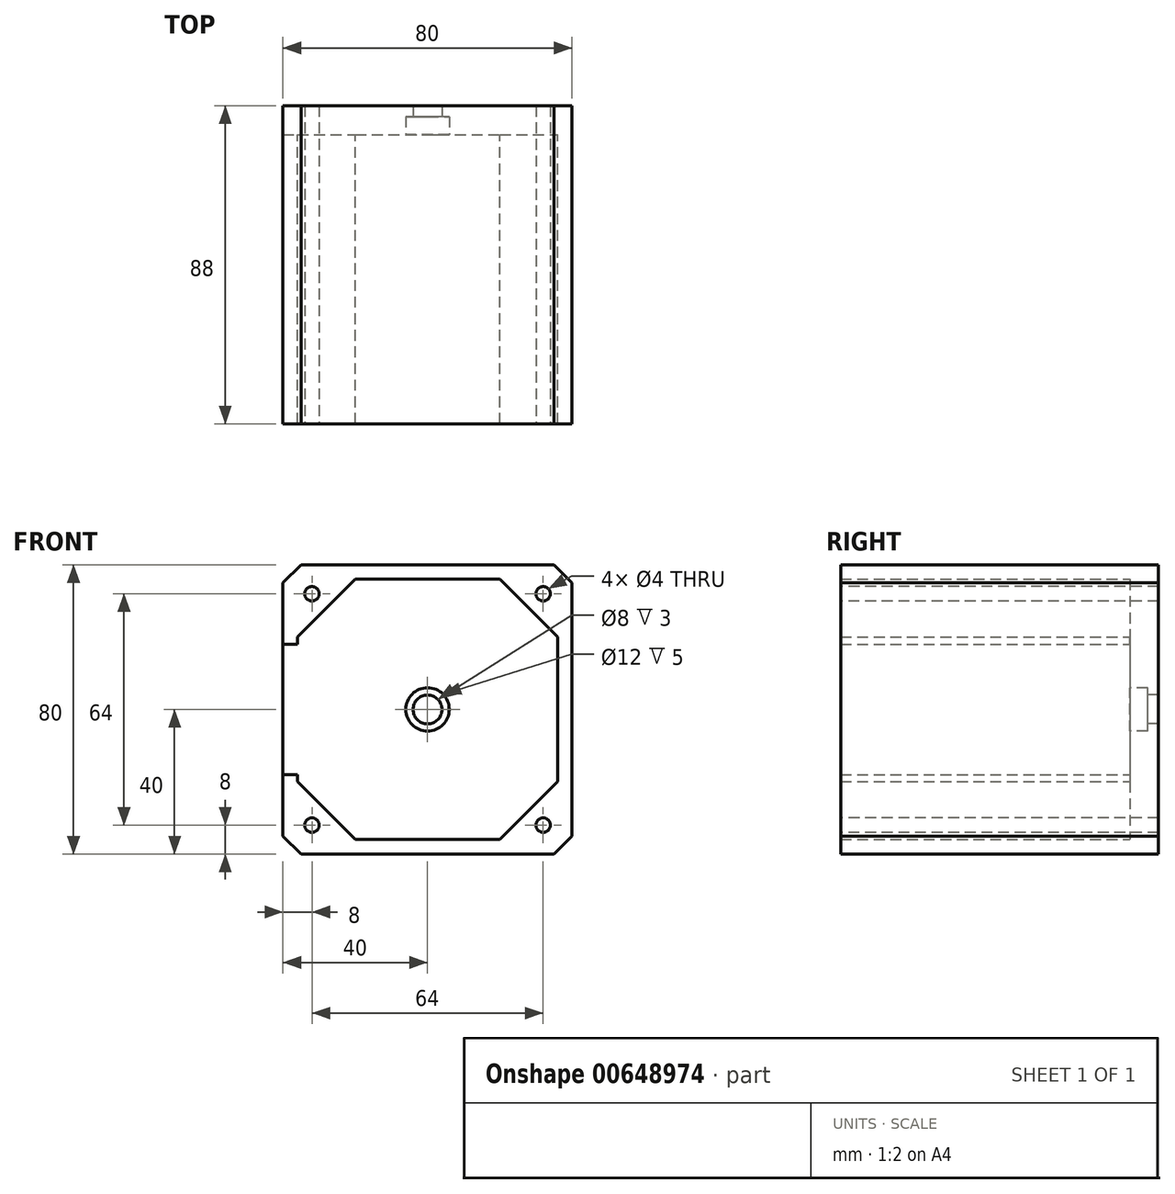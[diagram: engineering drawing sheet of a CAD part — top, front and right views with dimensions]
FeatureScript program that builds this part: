
annotation { "Feature Type Name" : "Feature", "Feature Type Description" : "" }
export const myFeature = defineFeature(function(context is Context, id is Id, definition is map)
    precondition{}
    {
        {
            var Q0;
            Q0=qCreatedBy(makeId("Front.planeOp"),FACE);
            var sketch = newSketch(context, id + "F0", { "sketchPlane" : qUnion([Q0])});
            skLineSegment(sketch, "E0.bottom", {"start": v(-40, 40) * mm, "end": v(40, 40) * mm});
            skLineSegment(sketch, "E0.top", {"start": v(-40, -40) * mm, "end": v(40, -40) * mm});
            skLineSegment(sketch, "E0.left", {"start": v(-40, 40) * mm, "end": v(-40, -40) * mm});
            skLineSegment(sketch, "E0.right", {"start": v(40, 40) * mm, "end": v(40, -40) * mm});
            skPoint(sketch, "E0.middle", {"position": v(0, 0) * mm});
            skSolve(sketch);
        }
        {
            var Q0;
            Q0 = qSketchRegion(id + "F0", true);
            extrude(context, id + "F1", {"entities" : qUnion([Q0]), "depth" : 8 * mm, "offsetDistance" : 25 * mm});
        }
        {
            var Q0;
            Q0=makeQuery(id+"F1.opExtrude","CAP_FACE",FACE,{"disambiguationData":[OSD([sQuery(id+"F0.wireOp",EDGE,"E0.bottom"),sQuery(id+"F0.wireOp",EDGE,"E0.top"),sQuery(id+"F0.wireOp",EDGE,"E0.left"),sQuery(id+"F0.wireOp",EDGE,"E0.right")])],"isStart":false});
            var sketch = newSketch(context, id + "F2", { "sketchPlane" : qUnion([Q0])});
            skCircle(sketch, "E1", {"center": v(0, 0) * mm, "radius": 4 * mm});
            skSolve(sketch);
        }
        {
            var Q0;
            Q0 = qSketchRegion(id + "F2", true);
            extrude(context, id + "F3", {"entities" : qUnion([Q0]), "operationType" : NewBodyOperationType.REMOVE, "endBound" : BoundingType.THROUGH_ALL, "oppositeDirection" : true, "depth" : 25 * mm, "offsetDistance" : 25 * mm});
        }
        {
            var Q0;
            Q0=makeQuery(id+"F1.opExtrude","CAP_FACE",FACE,{"disambiguationData":[OSD([sQuery(id+"F0.wireOp",EDGE,"E0.bottom"),sQuery(id+"F0.wireOp",EDGE,"E0.top"),sQuery(id+"F0.wireOp",EDGE,"E0.left"),sQuery(id+"F0.wireOp",EDGE,"E0.right")])],"isStart":false});
            var sketch = newSketch(context, id + "F4", { "sketchPlane" : qUnion([Q0])});
            skLineSegment(sketch, "E2.bottom", {"start": v(-40, 40) * mm, "end": v(40, 40) * mm});
            skLineSegment(sketch, "E2.top", {"start": v(-40, -40) * mm, "end": v(40, -40) * mm});
            skLineSegment(sketch, "E2.left", {"start": v(-40, 40) * mm, "end": v(-40, 18) * mm});
            skLineSegment(sketch, "E2.right", {"start": v(40, 40) * mm, "end": v(40, -40) * mm});
            skPoint(sketch, "E2.middle", {"position": v(0, 0) * mm});
            skLineSegment(sketch, "E3", {"start": v(-40, 18) * mm, "end": v(-36, 18) * mm});
            skLineSegment(sketch, "E4", {"start": v(-40, 0) * mm, "end": v(0, 0) * mm, "construction": true});
            skLineSegment(sketch, "E5", {"start": v(-36, 18) * mm, "end": v(-36, 20) * mm});
            skLineSegment(sketch, "E6", {"start": v(-36, 20) * mm, "end": v(-20, 36) * mm});
            skLineSegment(sketch, "E7", {"start": v(-20, 36) * mm, "end": v(20, 36) * mm});
            skLineSegment(sketch, "E8", {"start": v(20, 36) * mm, "end": v(36, 20) * mm});
            skLineSegment(sketch, "E9", {"start": v(36, 20) * mm, "end": v(36, 0) * mm});
            skLineSegment(sketch, "E10", {"start": v(36, 0) * mm, "end": v(0, 0) * mm, "construction": true});
            skLineSegment(sketch, "E11.MirrorCS", {"start": v(-40, -18) * mm, "end": v(-36, -18) * mm});
            skLineSegment(sketch, "E12.MirrorCS", {"start": v(-36, -18) * mm, "end": v(-36, -20) * mm});
            skLineSegment(sketch, "E13.MirrorCS", {"start": v(-36, -20) * mm, "end": v(-20, -36) * mm});
            skLineSegment(sketch, "E14.MirrorCS", {"start": v(-20, -36) * mm, "end": v(20, -36) * mm});
            skLineSegment(sketch, "E15.MirrorCS", {"start": v(36, -20) * mm, "end": v(36, 0) * mm});
            skLineSegment(sketch, "E16.MirrorCS", {"start": v(20, -36) * mm, "end": v(36, -20) * mm});
            skLineSegment(sketch, "E17.trimOffspring", {"start": v(-40, -18) * mm, "end": v(-40, -40) * mm});
            skSolve(sketch);
        }
        {
            var Q0;
            Q0 = qSketchRegion(id + "F4", true);
            extrude(context, id + "F5", {"entities" : qUnion([Q0]), "operationType" : NewBodyOperationType.ADD, "depth" : 80 * mm, "offsetDistance" : 25 * mm});
        }
        {
            var Q0;
            Q0=makeQuery(id+"F5.boolean.opBoolean","MERGE",EDGE,{"derivedFrom":[makeQuery(id+"F1.opExtrude","SWEPT_EDGE",EDGE,{"disambiguationData":[OSD([sQuery(id+"F0.wireOp",EDGE,"E0.bottom"),sQuery(id+"F0.wireOp",EDGE,"E0.left")])]}),makeQuery(id+"F5.opExtrude","SWEPT_EDGE",EDGE,{"disambiguationData":[OSD([sQuery(id+"F4.wireOp",EDGE,"E2.bottom"),sQuery(id+"F4.wireOp",EDGE,"E2.left")])]})]});
            var Q1;
            Q1=makeQuery(id+"F5.boolean.opBoolean","MERGE",EDGE,{"derivedFrom":[makeQuery(id+"F1.opExtrude","SWEPT_EDGE",EDGE,{"disambiguationData":[OSD([sQuery(id+"F0.wireOp",EDGE,"E0.bottom"),sQuery(id+"F0.wireOp",EDGE,"E0.right")])]}),makeQuery(id+"F5.opExtrude","SWEPT_EDGE",EDGE,{"disambiguationData":[OSD([sQuery(id+"F4.wireOp",EDGE,"E2.bottom"),sQuery(id+"F4.wireOp",EDGE,"E2.right")])]})]});
            var Q2;
            Q2=makeQuery(id+"F5.boolean.opBoolean","MERGE",EDGE,{"derivedFrom":[makeQuery(id+"F1.opExtrude","SWEPT_EDGE",EDGE,{"disambiguationData":[OSD([sQuery(id+"F0.wireOp",EDGE,"E0.top"),sQuery(id+"F0.wireOp",EDGE,"E0.left")])]}),makeQuery(id+"F5.opExtrude","SWEPT_EDGE",EDGE,{"disambiguationData":[OSD([sQuery(id+"F4.wireOp",EDGE,"E2.top"),sQuery(id+"F4.wireOp",EDGE,"E17.trimOffspring")])]})]});
            var Q3;
            Q3=makeQuery(id+"F5.boolean.opBoolean","MERGE",EDGE,{"derivedFrom":[makeQuery(id+"F1.opExtrude","SWEPT_EDGE",EDGE,{"disambiguationData":[OSD([sQuery(id+"F0.wireOp",EDGE,"E0.top"),sQuery(id+"F0.wireOp",EDGE,"E0.right")])]}),makeQuery(id+"F5.opExtrude","SWEPT_EDGE",EDGE,{"disambiguationData":[OSD([sQuery(id+"F4.wireOp",EDGE,"E2.top"),sQuery(id+"F4.wireOp",EDGE,"E2.right")])]})]});
            chamfer(context, id + "F6", {"entities" : qUnion([Q0, Q1, Q2, Q3]), "width" : 5 * mm, "tangentPropagation" : true});
        }
        {
            var Q0;
            Q0=makeQuery(id+"F5.opExtrude","CAP_FACE",FACE,{"disambiguationData":[OSD([sQuery(id+"F4.wireOp",EDGE,"E2.bottom"),sQuery(id+"F4.wireOp",EDGE,"E2.top"),sQuery(id+"F4.wireOp",EDGE,"E2.left"),sQuery(id+"F4.wireOp",EDGE,"E2.right"),sQuery(id+"F4.wireOp",EDGE,"E3"),sQuery(id+"F4.wireOp",EDGE,"E5"),sQuery(id+"F4.wireOp",EDGE,"E6"),sQuery(id+"F4.wireOp",EDGE,"E7"),sQuery(id+"F4.wireOp",EDGE,"E8"),sQuery(id+"F4.wireOp",EDGE,"E9"),sQuery(id+"F4.wireOp",EDGE,"E11.MirrorCS"),sQuery(id+"F4.wireOp",EDGE,"E12.MirrorCS"),sQuery(id+"F4.wireOp",EDGE,"E13.MirrorCS"),sQuery(id+"F4.wireOp",EDGE,"E14.MirrorCS"),sQuery(id+"F4.wireOp",EDGE,"E15.MirrorCS"),sQuery(id+"F4.wireOp",EDGE,"E16.MirrorCS"),sQuery(id+"F4.wireOp",EDGE,"E17.trimOffspring")])],"isStart":false});
            var sketch = newSketch(context, id + "F7", { "sketchPlane" : qUnion([Q0])});
            skCircle(sketch, "E18", {"center": v(-32, 32) * mm, "radius": 2 * mm});
            skCircle(sketch, "E19.1.0", {"center": v(-32, -32) * mm, "radius": 2 * mm});
            skCircle(sketch, "E19.2.0", {"center": v(32, -32) * mm, "radius": 2 * mm});
            skCircle(sketch, "E19.3.0", {"center": v(32, 32) * mm, "radius": 2 * mm});
            skPoint(sketch, "E19.center", {"position": v(0, 0) * mm});
            skSolve(sketch);
        }
        {
            var Q0;
            Q0 = qSketchRegion(id + "F7", true);
            extrude(context, id + "F8", {"entities" : qUnion([Q0]), "operationType" : NewBodyOperationType.REMOVE, "endBound" : BoundingType.THROUGH_ALL, "oppositeDirection" : true, "depth" : 25 * mm, "offsetDistance" : 25 * mm});
        }
        {
            var Q0;
            Q0=makeQuery(id+"F1.opExtrude","CAP_FACE",FACE,{"disambiguationData":[OSD([sQuery(id+"F0.wireOp",EDGE,"E0.bottom"),sQuery(id+"F0.wireOp",EDGE,"E0.top"),sQuery(id+"F0.wireOp",EDGE,"E0.left"),sQuery(id+"F0.wireOp",EDGE,"E0.right")])],"isStart":false});
            var sketch = newSketch(context, id + "F9", { "sketchPlane" : qUnion([Q0])});
            skCircle(sketch, "E20", {"center": v(0, 0) * mm, "radius": 6 * mm});
            skSolve(sketch);
        }
        {
            var Q0;
            Q0 = qSketchRegion(id + "F9", true);
            extrude(context, id + "F10", {"entities" : qUnion([Q0]), "operationType" : NewBodyOperationType.REMOVE, "oppositeDirection" : true, "depth" : 5 * mm, "offsetDistance" : 25 * mm});
        }
    });
